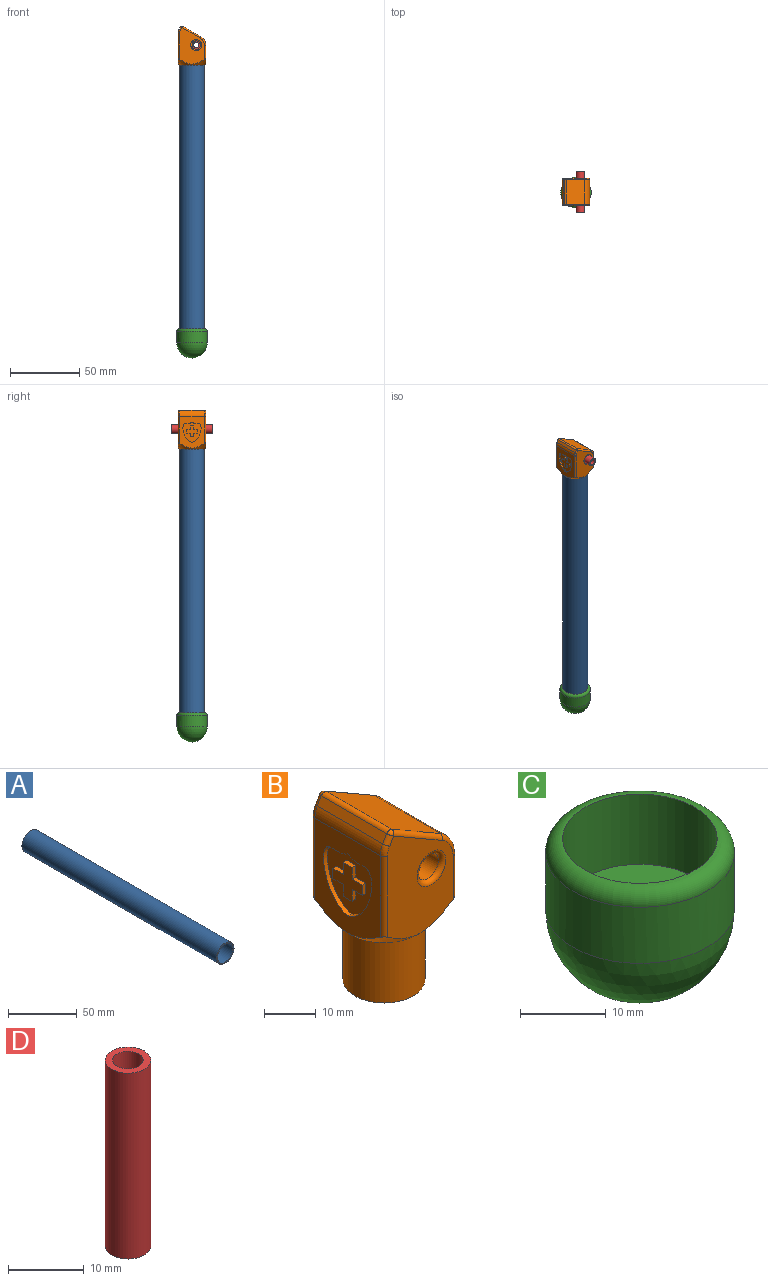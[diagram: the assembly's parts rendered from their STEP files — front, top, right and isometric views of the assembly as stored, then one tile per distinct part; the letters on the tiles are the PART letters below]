
ASSEMBLY  parts=4 mates=3
PART A: 4 faces, bbox 18x200x18 mm
  f0: cylinder r=8mm len=200mm, axis (0,1,0), area 10053.1mm2, adj f2,f3
  f1: cylinder r=9mm len=200mm, axis (0,1,0), area 11309.7mm2, adj f2,f3
  f2: plane 18x18mm, normal (0,-1,0), area 53.4mm2, adj f0,f1
  f3: plane 18x18mm, normal (0,1,0), area 53.4mm2, adj f0,f1
PART B: 48 faces, bbox 27.2x27.2x43.3 mm
  f0: plane 14.92x13.69mm, normal (-1,0,0), area 111.5mm2, adj f33,f34,f35,f36,f37,f38,f39,f40
  f1: plane 22.6x17.81mm, normal (-1,0,0), area 236.7mm2, adj f8,f14,f17,f24,f33,f34
  f2: plane 17.8x13.2mm, normal (0.5,0,0.87), area 271.3mm2, adj f15,f16,f21,f28
  f3: plane 26.45x17.81mm, normal (0,-1,0), area 321.4mm2, adj f8,f24,f25,f26,f28,f29,f30,f32
  f4: plane 26.45x17.81mm, normal (0,1,0), area 321.4mm2, adj f8,f17,f18,f19,f21,f22,f23,f31
  f5: plane 18x18mm, normal (0,0,-1), area 58.4mm2, adj f6,f8
  f6: cylinder r=7.9mm len=15.8mm, axis (0,0,1), area 744.6mm2, adj f5,f7
  f7: plane 15.8x15.8mm, normal (0,0,-1), area 117.5mm2, adj f6,f11
  f8: cone r=9mm half-angle=45deg, axis (0,0,1), area 193.3mm2, adj f1,f3,f4,f5,f10,f17,f23,f24
  f9: cylinder r=2.9mm len=17.8mm, axis (0,1,0), area 324.3mm2, adj f31,f32
  f10: plane 17.81x13.63mm, normal (1,0,0), area 221.1mm2, adj f8,f16,f23,f30
  f11: cylinder r=5mm len=24mm, axis (0,0,-1), area 754mm2, adj f7,f12
  f12: plane 10x10mm, normal (0,0,-1), area 78.5mm2, adj f11
  f13: plane 17.8x1.84mm, normal (-0.87,0,0.5), area 37.9mm2, adj f14,f15,f19,f26
  f14: cylinder r=5mm len=17.8mm, axis (0,1,0), area 46.6mm2, adj f1,f13,f18,f25
  f15: cylinder r=1mm len=17.8mm, axis (0,-1,0), area 28mm2, adj f2,f13,f20,f27
  f16: cylinder r=7mm len=17.8mm, axis (0,-1,0), area 130.5mm2, adj f2,f10,f22,f29
  f17: cylinder r=1mm len=19.19mm, axis (0,0,-1), area 29.9mm2, adj f1,f4,f8,f18
  f18: torus R=4mm, axis (0,-1,0), area 3.8mm2, adj f4,f14,f17,f19
  f19: cylinder r=1mm len=2.34mm, axis (0.5,0,0.87), area 3.3mm2, adj f4,f13,f18,f20
  f20: sphere r=1mm, area 1.6mm2, adj f15,f19,f21
  f21: cylinder r=1mm len=13.7mm, axis (-0.87,0,0.5), area 23.9mm2, adj f2,f4,f20,f22
  f22: torus R=6mm, axis (0,-1,0), area 10.9mm2, adj f4,f16,f21,f23
  f23: cylinder r=1mm len=10.21mm, axis (0,0,1), area 15.8mm2, adj f4,f8,f10,f22
  f24: cylinder r=1mm len=19.19mm, axis (0,0,1), area 29.9mm2, adj f1,f3,f8,f25
  f25: torus R=4mm, axis (0,-1,0), area 3.8mm2, adj f3,f14,f24,f26
  f26: cylinder r=1mm len=2.34mm, axis (-0.5,0,-0.87), area 3.3mm2, adj f3,f13,f25,f27
  f27: sphere r=1mm, area 1.6mm2, adj f15,f26,f28
  f28: cylinder r=1mm len=13.7mm, axis (0.87,0,-0.5), area 23.9mm2, adj f2,f3,f27,f29
  f29: torus R=6mm, axis (0,-1,0), area 10.9mm2, adj f3,f16,f28,f30
  f30: cylinder r=1mm len=10.21mm, axis (0,0,-1), area 15.8mm2, adj f3,f8,f10,f29
  f31: torus R=3.9mm, axis (0,-1,0), area 32.2mm2, adj f4,f9
  f32: torus R=3.9mm, axis (0,-1,0), area 32.2mm2, adj f3,f9
  f33: extruded ~14.6x6.53mm, area 22.2mm2, adj f0,f1,f34
  f34: extruded ~14.6x6.53mm, area 22.2mm2, adj f0,f1,f33
  f35: plane 2.4x1mm, normal (0,1,0), area 2.4mm2, adj f0,f36,f46,f47
  f36: plane 2.8x1mm, normal (0,0,-1), area 2.8mm2, adj f0,f35,f37,f47
  f37: plane 2.8x1mm, normal (0,1,0), area 2.8mm2, adj f0,f36,f38,f47
  f38: plane 2.4x1mm, normal (0,0,-1), area 2.4mm2, adj f0,f37,f39,f47
  f39: plane 2.8x1mm, normal (0,-1,0), area 2.8mm2, adj f0,f38,f40,f47
  f40: plane 2.8x1mm, normal (0,0,-1), area 2.8mm2, adj f0,f39,f41,f47
  f41: plane 2.4x1mm, normal (0,-1,0), area 2.4mm2, adj f0,f40,f42,f47
  f42: plane 2.8x1mm, normal (0,0,1), area 2.8mm2, adj f0,f41,f43,f47
  f43: plane 2.8x1mm, normal (0,-1,0), area 2.8mm2, adj f0,f42,f44,f47
  f44: plane 2.4x1mm, normal (0,0,1), area 2.4mm2, adj f0,f43,f45,f47
  f45: plane 2.8x1mm, normal (0,1,0), area 2.8mm2, adj f0,f44,f46,f47
  f46: plane 2.8x1mm, normal (0,0,1), area 2.8mm2, adj f0,f35,f45,f47
  f47: plane 8x8mm, normal (-1,0,0), area 32.6mm2, adj f35,f36,f37,f38,f39,f40,f41,f42
PART C: 5 faces, bbox 23.8x23.8x21 mm
  f0: sphere r=11mm, area 760.3mm2, adj f3
  f1: plane 18x18mm, normal (0,0,1), area 254.5mm2, adj f2
  f2: cylinder r=9mm len=18mm, axis (0,0,-1), area 565.5mm2, adj f1,f4
  f3: cylinder r=11mm len=22mm, axis (0,0,-1), area 552.9mm2, adj f0,f4
  f4: torus R=9mm, axis (0,0,1), area 202.8mm2, adj f2,f3
PART D: 4 faces, bbox 6x6x30 mm
  f0: cylinder r=2mm len=30mm, axis (0,0,-1), area 377mm2, adj f2,f3
  f1: cylinder r=3mm len=30mm, axis (0,0,-1), area 565.5mm2, adj f2,f3
  f2: plane 6x6mm, normal (0,0,1), area 15.7mm2, adj f0,f1
  f3: plane 6x6mm, normal (0,0,-1), area 15.7mm2, adj f0,f1
PLACE A rot(axis=(1,0,0),90deg) t=(-14.44,-8.5,-5.04)mm
PLACE B t=(-4.54,1.4,-5.04)mm
PLACE C t=(-14.44,-8.5,-205.04)mm
PLACE D rot(axis=(1,0,0),90deg) t=(-11.44,6.5,9.55)mm
MATE revolute C.f2 <-> A.f0  axis (0,0,1) through (-14.44,-8.5,-205.04)mm
MATE fastened B.f9 <-> D.f0  axis (0,-1,0) through (-11.44,-18.4,9.55)mm
MATE revolute A.f0 <-> B.f6  axis (0,0,1) through (-14.44,-8.5,-5.04)mm
